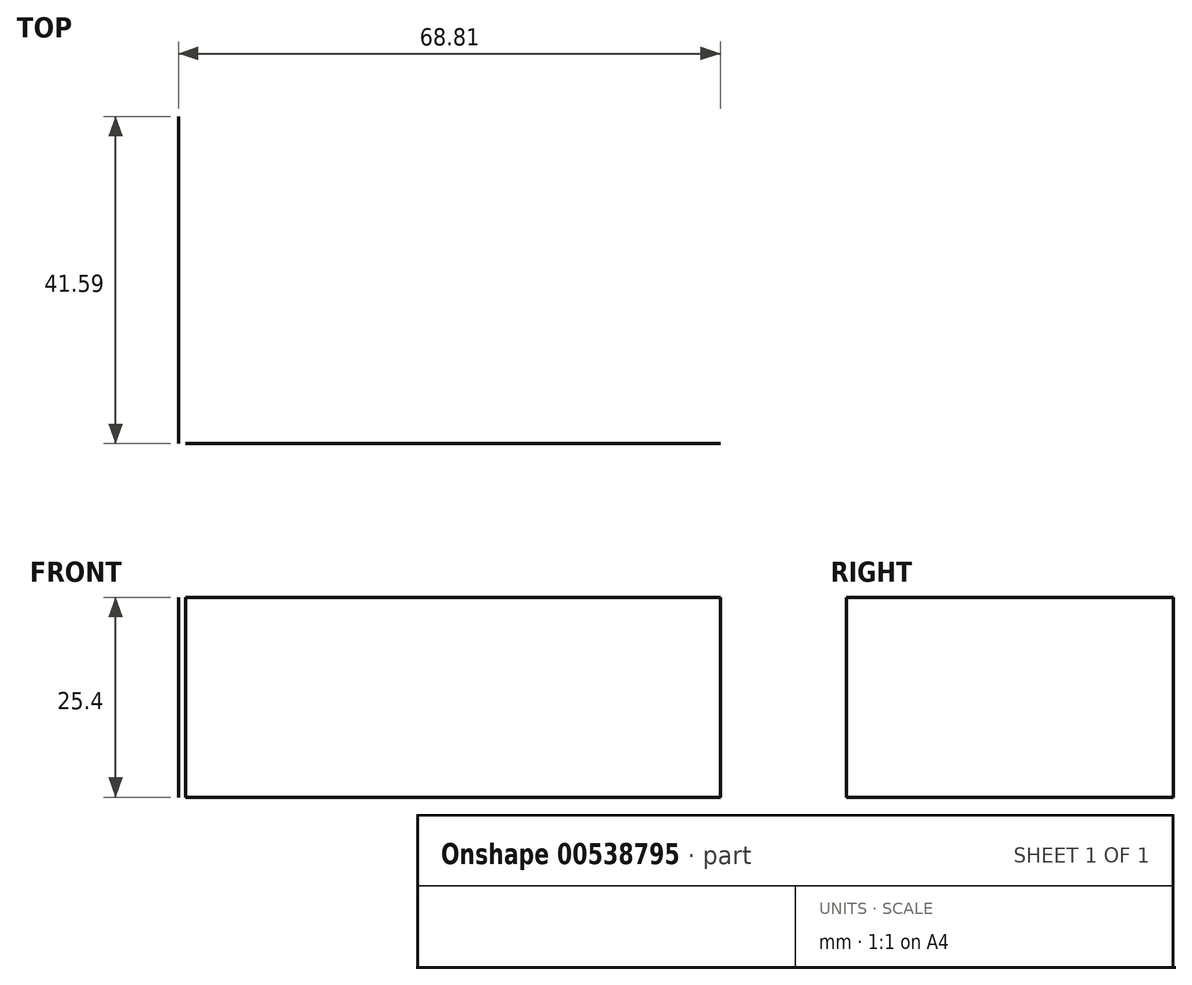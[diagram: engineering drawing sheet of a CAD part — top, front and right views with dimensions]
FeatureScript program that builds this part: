
annotation { "Feature Type Name" : "Feature", "Feature Type Description" : "" }
export const myFeature = defineFeature(function(context is Context, id is Id, definition is map)
    precondition{}
    {
        {
            var Q0;
            Q0=qCreatedBy(makeId("Top.planeOp"),FACE);
            var sketch = newSketch(context, id + "F0", { "sketchPlane" : qUnion([Q0])});
            skLineSegment(sketch, "E0", {"start": v(-68.8, 0) * mm, "end": v(-68.8, 41.59) * mm});
            skLineSegment(sketch, "E1", {"start": v(-68.8, 41.59) * mm, "end": v(-68.8, 0) * mm});
            skLineSegment(sketch, "E2", {"start": v(-68.8, 0) * mm, "end": v(0, 0) * mm});
            skSolve(sketch);
        }
        {
            var Q0;
            Q0=sQuery(id+"F0.wireOp",EDGE,"E1");
            extrude(context, id + "F1", {"bodyType" : ToolBodyType.SURFACE, "surfaceEntities" : qUnion([Q0]), "depth" : 25.4 * mm, "offsetDistance" : 25.4 * mm});
        }
        {
            var Q0;
            Q0=qCreatedBy(makeId("Top.planeOp"),FACE);
            var sketch = newSketch(context, id + "F2", { "sketchPlane" : qUnion([Q0])});
            skLineSegment(sketch, "E3", {"start": v(-67.92, 0) * mm, "end": v(0, 0) * mm});
            skSolve(sketch);
        }
        {
            var Q0;
            Q0=sQuery(id+"F2.wireOp",EDGE,"E3");
            extrude(context, id + "F3", {"bodyType" : ToolBodyType.SURFACE, "surfaceEntities" : qUnion([Q0]), "depth" : 25.4 * mm, "offsetDistance" : 25.4 * mm});
        }
    });
